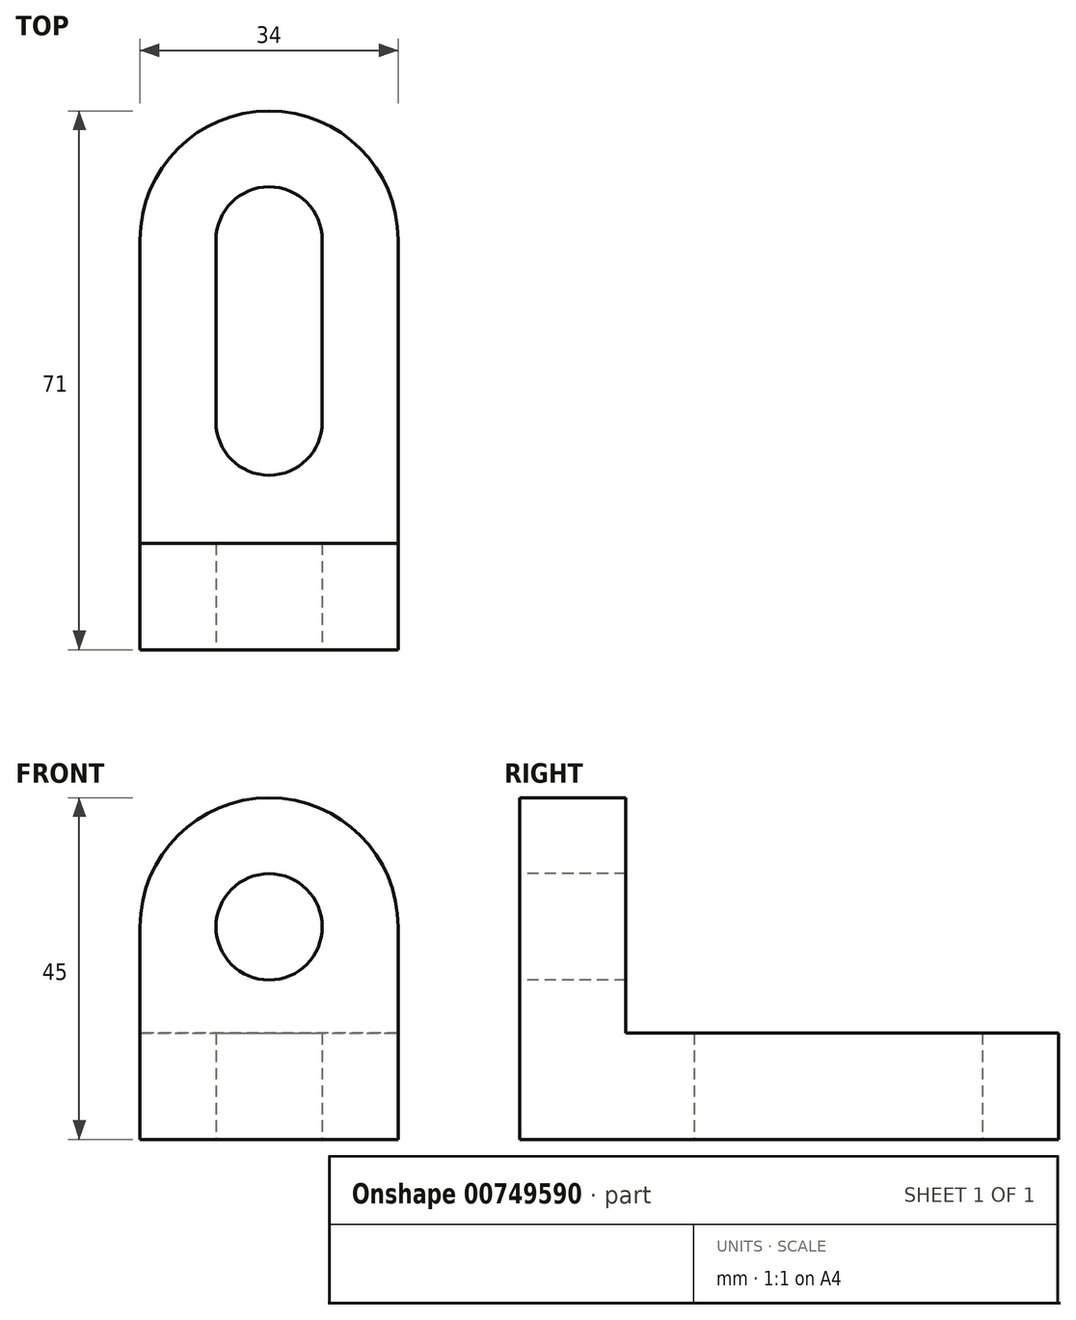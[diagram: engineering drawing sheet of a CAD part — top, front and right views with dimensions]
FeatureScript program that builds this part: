
annotation { "Feature Type Name" : "Feature", "Feature Type Description" : "" }
export const myFeature = defineFeature(function(context is Context, id is Id, definition is map)
    precondition{}
    {
        {
            var Q0;
            Q0=qCreatedBy(makeId("Top.planeOp"),FACE);
            var sketch = newSketch(context, id + "F0", { "sketchPlane" : qUnion([Q0])});
            skLineSegment(sketch, "E0.bottom", {"start": v(0, 0) * mm, "end": v(34, 0) * mm});
            skLineSegment(sketch, "E0.left", {"start": v(0, 0) * mm, "end": v(0, 54) * mm});
            skLineSegment(sketch, "E0.right", {"start": v(34, 0) * mm, "end": v(34, 54) * mm});
            skArc(sketch, "E1", {"start": v(34, 54) * mm, "mid": v(17, 71) * mm, "end": v(0, 54) * mm});
            skLineSegment(sketch, "E2", {"start": v(24, 54) * mm, "end": v(24, 30) * mm});
            skLineSegment(sketch, "E3", {"start": v(10, 30) * mm, "end": v(10, 54) * mm});
            skArc(sketch, "E4", {"start": v(10, 30) * mm, "mid": v(17, 23) * mm, "end": v(24, 30) * mm});
            skArc(sketch, "E5", {"start": v(24, 54) * mm, "mid": v(17, 61) * mm, "end": v(10, 54) * mm});
            skSolve(sketch);
        }
        {
            var Q0;
            Q0=makeQuery(id+"F0.imprint","IMPRINT",FACE,{"disambiguationData":[TD([[makeQuery(id+"F0.imprint","IMPRINT",EDGE,{"derivedFrom":sQuery(id+"F0.wireOp",EDGE,"E0.bottom")}),1.0]])]});
            extrude(context, id + "F1", {"entities" : qUnion([Q0]), "depth" : 14 * mm, "offsetDistance" : 25 * mm});
        }
        {
            var Q0;
            Q0=makeQuery(id+"F1.opExtrude","SWEPT_FACE",FACE,{"disambiguationData":[OSD([sQuery(id+"F0.wireOp",EDGE,"E0.bottom")])]});
            var sketch = newSketch(context, id + "F2", { "sketchPlane" : qUnion([Q0])});
            skLineSegment(sketch, "E6", {"start": v(0, 14) * mm, "end": v(0, 28) * mm});
            skLineSegment(sketch, "E7", {"start": v(34, 28) * mm, "end": v(34, 14) * mm});
            skLineSegment(sketch, "E8", {"start": v(34, 14) * mm, "end": v(0, 14) * mm});
            skArc(sketch, "E9", {"start": v(34, 28) * mm, "mid": v(17, 45) * mm, "end": v(0, 28) * mm});
            skCircle(sketch, "E10", {"center": v(17, 28) * mm, "radius": 7 * mm});
            skSolve(sketch);
        }
        {
            var Q0;
            Q0=makeQuery(id+"F2.imprint","IMPRINT",FACE,{"disambiguationData":[TD([[makeQuery(id+"F2.imprint","IMPRINT",EDGE,{"derivedFrom":sQuery(id+"F2.wireOp",EDGE,"E6")}),-1.0]])]});
            extrude(context, id + "F3", {"entities" : qUnion([Q0]), "operationType" : NewBodyOperationType.ADD, "oppositeDirection" : true, "depth" : 14 * mm, "offsetDistance" : 25 * mm});
        }
    });
